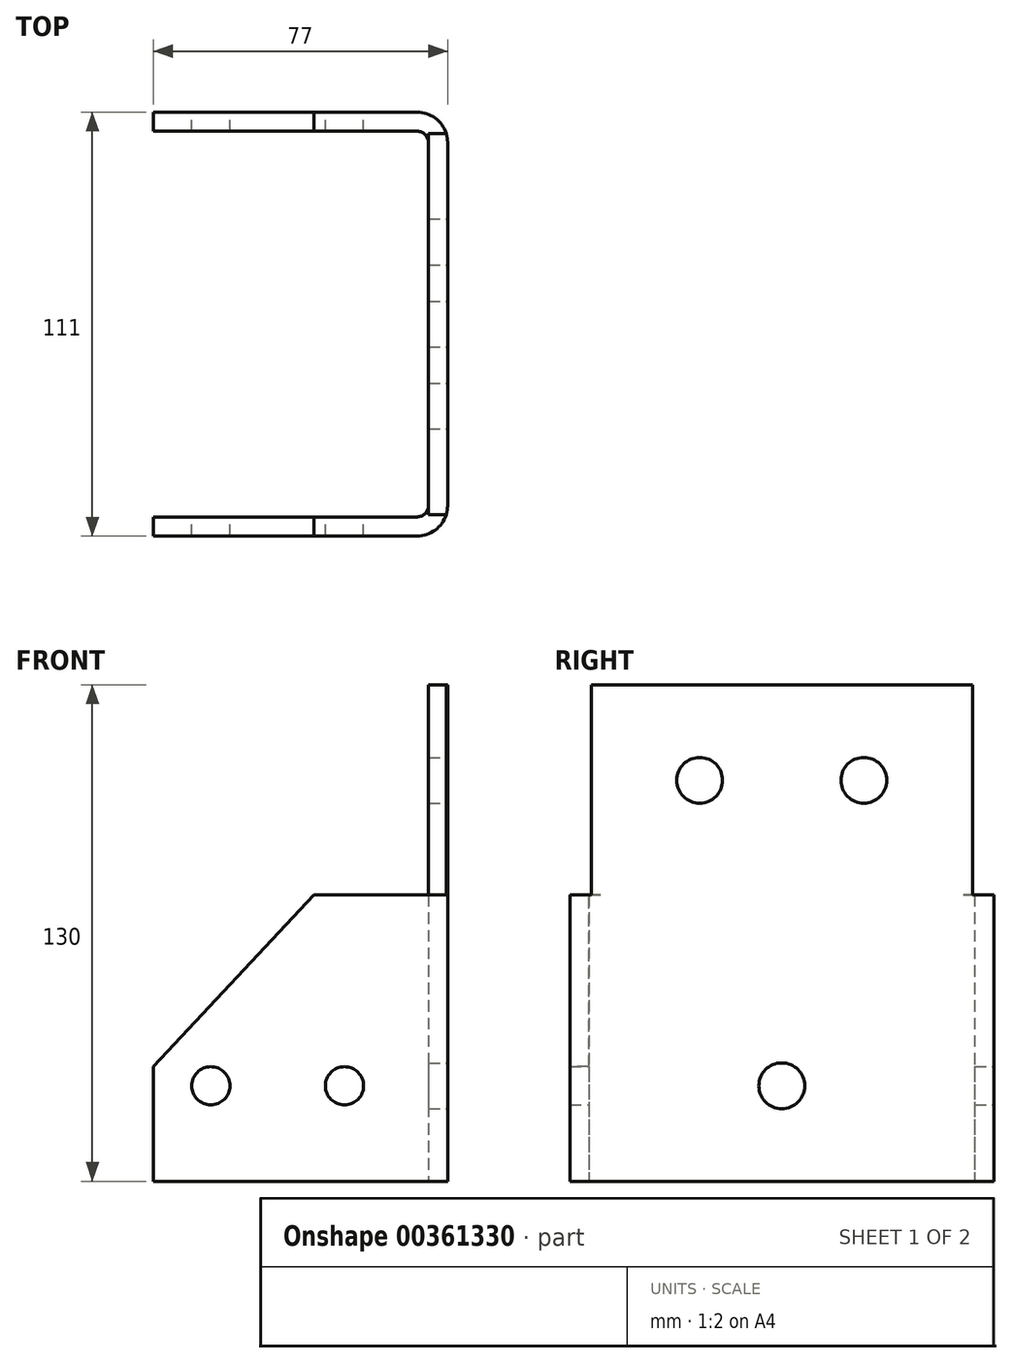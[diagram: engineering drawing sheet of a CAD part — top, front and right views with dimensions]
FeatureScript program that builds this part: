
annotation { "Feature Type Name" : "Feature", "Feature Type Description" : "" }
export const myFeature = defineFeature(function(context is Context, id is Id, definition is map)
    precondition{}
    {
        {
            var Q0;
            Q0=qCreatedBy(makeId("Top.planeOp"),FACE);
            var sketch = newSketch(context, id + "F0", { "sketchPlane" : qUnion([Q0])});
            skLineSegment(sketch, "E0", {"start": v(0, 0) * mm, "end": v(0, -5) * mm});
            skLineSegment(sketch, "E1", {"start": v(0, 0) * mm, "end": v(69, 0) * mm});
            skLineSegment(sketch, "E2", {"start": v(77, -8) * mm, "end": v(77, -103) * mm});
            skLineSegment(sketch, "E3", {"start": v(69, -111) * mm, "end": v(0, -111) * mm});
            skLineSegment(sketch, "E4", {"start": v(0, -111) * mm, "end": v(0, -106) * mm});
            skLineSegment(sketch, "E5", {"start": v(0, -106) * mm, "end": v(69, -106) * mm});
            skLineSegment(sketch, "E6", {"start": v(0, -5) * mm, "end": v(69, -5) * mm});
            skLineSegment(sketch, "E7", {"start": v(72, -32.97) * mm, "end": v(72, -8) * mm});
            skLineSegment(sketch, "E8", {"start": v(72, -32.97) * mm, "end": v(72, -103) * mm});
            skPoint(sketch, "E9.orphan", {"position": v(122.2, -5) * mm});
            skPoint(sketch, "E10.orphan", {"position": v(122.2, -106) * mm});
            skPoint(sketch, "E11.visualSharp", {"position": v(77, 0) * mm});
            skArc(sketch, "E11.filletArc", {"start": v(77, -8) * mm, "mid": v(74.66, -2.34) * mm, "end": v(69, 0) * mm});
            skPoint(sketch, "E12.visualSharp", {"position": v(77, -111) * mm});
            skArc(sketch, "E12.filletArc", {"start": v(69, -111) * mm, "mid": v(74.66, -108.66) * mm, "end": v(77, -103) * mm});
            skPoint(sketch, "E13.visualSharp", {"position": v(72, -106) * mm});
            skArc(sketch, "E13.filletArc", {"start": v(69, -106) * mm, "mid": v(71.12, -105.12) * mm, "end": v(72, -103) * mm});
            skPoint(sketch, "E14.visualSharp", {"position": v(72, -5) * mm});
            skArc(sketch, "E14.filletArc", {"start": v(72, -8) * mm, "mid": v(71.12, -5.88) * mm, "end": v(69, -5) * mm});
            skSolve(sketch);
        }
        {
            var Q0;
            Q0 = qSketchRegion(id + "F0", true);
            extrude(context, id + "F1", {"entities" : qUnion([Q0]), "depth" : 130 * mm});
        }
        {
            var Q0;
            Q0=makeQuery(id+"F1.opExtrude","SWEPT_FACE",FACE,{"disambiguationData":[OSD([sQuery(id+"F0.wireOp",EDGE,"E1")])]});
            var sketch = newSketch(context, id + "F2", { "sketchPlane" : qUnion([Q0])});
            skLineSegment(sketch, "E15", {"start": v(0, 130) * mm, "end": v(-72, 130) * mm});
            skLineSegment(sketch, "E16", {"start": v(-72, 130) * mm, "end": v(-72, 75) * mm});
            skLineSegment(sketch, "E17", {"start": v(-72, 75) * mm, "end": v(-42, 75) * mm});
            skLineSegment(sketch, "E18", {"start": v(-42, 75) * mm, "end": v(0, 30) * mm});
            skLineSegment(sketch, "E19", {"start": v(0, 30) * mm, "end": v(0, 130) * mm});
            skSolve(sketch);
        }
        {
            var Q0;
            Q0 = qSketchRegion(id + "F2", true);
            extrude(context, id + "F3", {"entities" : qUnion([Q0]), "operationType" : NewBodyOperationType.REMOVE, "oppositeDirection" : true, "depth" : 25 * mm});
        }
        {
            var Q0;
            Q0=makeQuery(id+"F1.opExtrude","SWEPT_FACE",FACE,{"disambiguationData":[OSD([sQuery(id+"F0.wireOp",EDGE,"E3")])]});
            var sketch = newSketch(context, id + "F4", { "sketchPlane" : qUnion([Q0])});
            skLineSegment(sketch, "E20", {"start": v(0, 130) * mm, "end": v(72, 130) * mm});
            skLineSegment(sketch, "E21", {"start": v(0, 0) * mm, "end": v(0, 30) * mm});
            skLineSegment(sketch, "E22", {"start": v(0, 130) * mm, "end": v(0, 75) * mm});
            skLineSegment(sketch, "E23", {"start": v(72, 130) * mm, "end": v(72, 75) * mm});
            skLineSegment(sketch, "E24", {"start": v(72, 75) * mm, "end": v(42, 75) * mm});
            skLineSegment(sketch, "E25", {"start": v(42, 75) * mm, "end": v(0, 30) * mm});
            skLineSegment(sketch, "E26", {"start": v(0, 75) * mm, "end": v(0, 30) * mm});
            skSolve(sketch);
        }
        {
            var Q0;
            Q0 = qSketchRegion(id + "F4", true);
            extrude(context, id + "F5", {"entities" : qUnion([Q0]), "operationType" : NewBodyOperationType.REMOVE, "oppositeDirection" : true, "depth" : 25 * mm});
        }
        {
            var Q0;
            Q0=makeQuery(id+"F1.opExtrude","SWEPT_FACE",FACE,{"disambiguationData":[OSD([sQuery(id+"F0.wireOp",EDGE,"E1")])]});
            var sketch = newSketch(context, id + "F6", { "sketchPlane" : qUnion([Q0])});
            skCircle(sketch, "E27", {"center": v(-15, 25) * mm, "radius": 5 * mm});
            skCircle(sketch, "E28", {"center": v(-50, 25) * mm, "radius": 5 * mm});
            skPoint(sketch, "E29.end.orphan", {"position": v(-15, 0) * mm});
            skPoint(sketch, "E30.end.orphan", {"position": v(0, 25) * mm});
            skSolve(sketch);
        }
        {
            var Q0;
            Q0 = qSketchRegion(id + "F6", true);
            extrude(context, id + "F7", {"entities" : qUnion([Q0]), "operationType" : NewBodyOperationType.REMOVE, "oppositeDirection" : true, "depth" : 200 * mm});
        }
        {
            var Q0;
            Q0=makeQuery(id+"F1.opExtrude","SWEPT_FACE",FACE,{"disambiguationData":[OSD([sQuery(id+"F0.wireOp",EDGE,"E2")])]});
            var sketch = newSketch(context, id + "F8", { "sketchPlane" : qUnion([Q0])});
            skCircle(sketch, "E31", {"center": v(-55.5, 25) * mm, "radius": 6 * mm});
            skLineSegment(sketch, "E32", {"start": v(-8, 130) * mm, "end": v(-8, 105) * mm});
            skPoint(sketch, "E33.end.orphan", {"position": v(-55.5, 0) * mm});
            skSolve(sketch);
        }
        {
            var Q0;
            Q0 = qSketchRegion(id + "F8", true);
            extrude(context, id + "F9", {"entities" : qUnion([Q0]), "operationType" : NewBodyOperationType.REMOVE, "oppositeDirection" : true, "depth" : 25 * mm});
        }
        {
            var Q0;
            Q0=makeQuery(id+"F1.opExtrude","CAP_FACE",FACE,{"disambiguationData":[OSD([sQuery(id+"F0.wireOp",EDGE,"E0"),sQuery(id+"F0.wireOp",EDGE,"E1"),sQuery(id+"F0.wireOp",EDGE,"E2"),sQuery(id+"F0.wireOp",EDGE,"E3"),sQuery(id+"F0.wireOp",EDGE,"E4"),sQuery(id+"F0.wireOp",EDGE,"E5"),sQuery(id+"F0.wireOp",EDGE,"E6"),sQuery(id+"F0.wireOp",EDGE,"E7"),sQuery(id+"F0.wireOp",EDGE,"E8"),sQuery(id+"F0.wireOp",EDGE,"E11.filletArc"),sQuery(id+"F0.wireOp",EDGE,"E12.filletArc"),sQuery(id+"F0.wireOp",EDGE,"E13.filletArc"),sQuery(id+"F0.wireOp",EDGE,"E14.filletArc")])],"isStart":false});
            var sketch = newSketch(context, id + "F10", { "sketchPlane" : qUnion([Q0])});
            skLineSegment(sketch, "E34", {"start": v(77, -5.58) * mm, "end": v(72, -5.58) * mm});
            skArc(sketch, "E35", {"start": v(76.63, -5.58) * mm, "mid": v(74.87, -2.57) * mm, "end": v(72, -0.58) * mm});
            skPoint(sketch, "E36.end.orphan", {"position": v(77, -0.58) * mm});
            skLineSegment(sketch, "E37", {"start": v(72, -5.58) * mm, "end": v(72, -0.58) * mm});
            skLineSegment(sketch, "E38", {"start": v(77, -105.42) * mm, "end": v(72, -105.42) * mm});
            skLineSegment(sketch, "E39", {"start": v(72, -105.42) * mm, "end": v(72, -110.42) * mm});
            skPoint(sketch, "E40.end.orphan", {"position": v(77, -110.42) * mm});
            skArc(sketch, "E41", {"start": v(72, -110.42) * mm, "mid": v(74.87, -108.43) * mm, "end": v(76.63, -105.42) * mm});
            skSolve(sketch);
        }
        {
            var Q0;
            Q0 = qSketchRegion(id + "F10", true);
            extrude(context, id + "F11", {"entities" : qUnion([Q0]), "operationType" : NewBodyOperationType.REMOVE, "oppositeDirection" : true, "depth" : 55 * mm});
        }
        {
            var Q0;
            Q0=makeQuery(id+"F1.opExtrude","SWEPT_FACE",FACE,{"disambiguationData":[OSD([sQuery(id+"F0.wireOp",EDGE,"E2")])]});
            var sketch = newSketch(context, id + "F12", { "sketchPlane" : qUnion([Q0])});
            skCircle(sketch, "E42", {"center": v(-77, 105) * mm, "radius": 6 * mm});
            skCircle(sketch, "E43", {"center": v(-34, 105) * mm, "radius": 6 * mm});
            skPoint(sketch, "E44.start.orphan", {"position": v(-55.5, 25) * mm});
            skLineSegment(sketch, "E45", {"start": v(-77, 105) * mm, "end": v(-77, 25) * mm});
            skLineSegment(sketch, "E46", {"start": v(-77, 25) * mm, "end": v(-55.5, 25) * mm});
            skSolve(sketch);
        }
        {
            var Q0;
            Q0 = qSketchRegion(id + "F12", true);
            extrude(context, id + "F13", {"entities" : qUnion([Q0]), "operationType" : NewBodyOperationType.REMOVE, "oppositeDirection" : true, "depth" : 25 * mm});
        }
    });
